# Revit family: Faucet-Lavatory-KOHLER-Finial_Traditional-K-8670T
name_source: partatom
category: Plumbing Fixtures
revit_build: Autodesk Revit 2017 (Build: 20160225_1515(x64)
units: mm (PartAtom-declared; Revit-internal decimal feet)

## family parameters
Cut with Voids When Loaded = No
Host = Face
OmniClass Number = 23.31.11.00
OmniClass Title = Faucets
Part Type = Normal
Room Calculation Point = No
Round Connector Dimension = Use Diameter
Shared = No

## types (6) — shared parameters
ADA Compliant = No
Assembly Code = D2010
CW Connection = Yes
Cold Water Inlet = Cold Water Inlet
Date Modified = 08/14/2020
Default Elevation = 36"
Description = TRADITIONAL LAV 8
Drain Included = Yes
Flow Rate = 0 GPM
HW Connection = Yes
Handle Clearance = 3 1/4"
Height = 6 1/2"
Hot Water Inlet = Hot Water Inlet
Length = 5"
Manufacturer = KOHLER Co.
Master Format 2014 = 22 41 39
Master Format 2014 Name = Residential Faucets, Supplies, and Trim
Material = Premium Metal Construction
Pressure = 0.00 psi
Product Documentation Link = https://files.kohler.com.cn
Product Name = Finial_Traditional
Product Page URL = https://www.kohler.com.cn
Spout Reach = 5"
URL = http://www.kohler.com.cn
Vent Connection = No
Waste Connection = No
Waste Water Outlet = Waste Water Outlet
WaterSense Certified = No

## per-type parameters (varying)
| type | Body Finish | Finish | Handel Finish | Model | Type |
| CP-Polished Chrome | Kohler-Metal-CP-Polished_Chrome | Kohler-Metal-CP-Polished_Chrome | Kohler-Metal-CP-Polished_Chrome | K-8670T-4M-CP | 1 |
| AF-Flange Gold | Kohler-Metal-AF-Vibrant_French_Gold | Kohler-Metal-AF-Vibrant_French_Gold | Kohler-Metal-AF-Vibrant_French_Gold | K-8670T-4M-AF | 2 |
| SN-Champagne Gold | Kohler-Metal-SN-Vibrant_Polished_Nickel | Kohler-Metal-SN-Vibrant_Polished_Nickel | Kohler-Metal-SN-Vibrant_Polished_Nickel | K-8670T-4M-SN | 3 |
| BN-Roman Silver | Kohler-Metal-BN-Vibrant_Brushed_Nickel | Kohler-Metal-BN-Vibrant_Brushed_Nickel | Kohler-Metal-BN-Vibrant_Brushed_Nickel | K-8670T-4M-BN | 4 |
| White Handle, CP- Polished Chrome | Kohler-Metal-CP-Polished_Chrome | Kohler-Metal-CP-Polished_Chrome | Kohler-Metal-0-White | K-8670T-4P-CP | 6 |
| R2B-Black Yaojin | Kohler-Metal-BL-Matte_Black | Kohler-Metal-RGD-Rose_Gold | Kohler-Metal-RGD-Rose_Gold | K-8670T-4M-R2B | 5 |

## geometry (parser evidence)
native form markers: Sweep x7
no freeform markers — native parametric forms only
